# Revit family: Faucet-Single_Handle-GROHE-Plus-23956003
name_source: partatom
category: Plumbing Fixtures
revit_build: Autodesk Revit 2018 (Build: 20170223_1515(x64)
units: mm (PartAtom-declared; Revit-internal decimal feet)

## family parameters
Always vertical = No
Cut with Voids When Loaded = No
OmniClass Number = 23.45.55.14
OmniClass Title = Single Faucets
Part Type = Normal
Room Calculation Point = No
Round Connector Dimension = Use Diameter
Shared = Yes
Work Plane-Based = Yes

## types (1)
- 23956003
    Assembly Code = D2020300
    Body Material = Metal-Grohe-StarLight-Chrome
    CW Connection = No
    CWFU = 1.5
    Connection Type = 1" Tempered Connection
    Default Elevation = 0"
    Description = Elegant or minimalist, the GROHE Plus Centerset Bathroom Faucet combines the clean, linear angles of a cube with the gentle curves of a circle making it a distinctive choice no matter the design aesthetic. Engineered to bring comfort and convenience to your bathroom, the Plus Centerset faucet features GROHE SilkMove® for smooth, precise handle motion and the durable GROHE StarLight® coating for easy care and lasting beauty.
    Flow Rate = 1.2 gpm (4.56 L/min)
    HW Connection = No
    HWFU = 1.5
    Height = 7 1/2"
    Installation Type = Deck-Mounted
    Manufacturer = Grohe
    Model = 23956003
    Price = Prices may vary. Please consult Manufacturer Representative for most up-to-date price list.
    Product Documentation Link = https://americanstandard.box.com
    Product Page URL = https://www.grohe.ca
    Tempered Water Connection Diameter = 1"
    Tempered Water Connection Radius = 1/2"
    URL = https://www.grohe.ca
    Vent Connection = No
    WFU = 2
    Warranty Documentation Link = https://www.grohe.ca
    Waste Connection = No
    Width = 2"

## geometry (parser evidence)
native form markers: Sweep x2
no freeform markers — native parametric forms only
